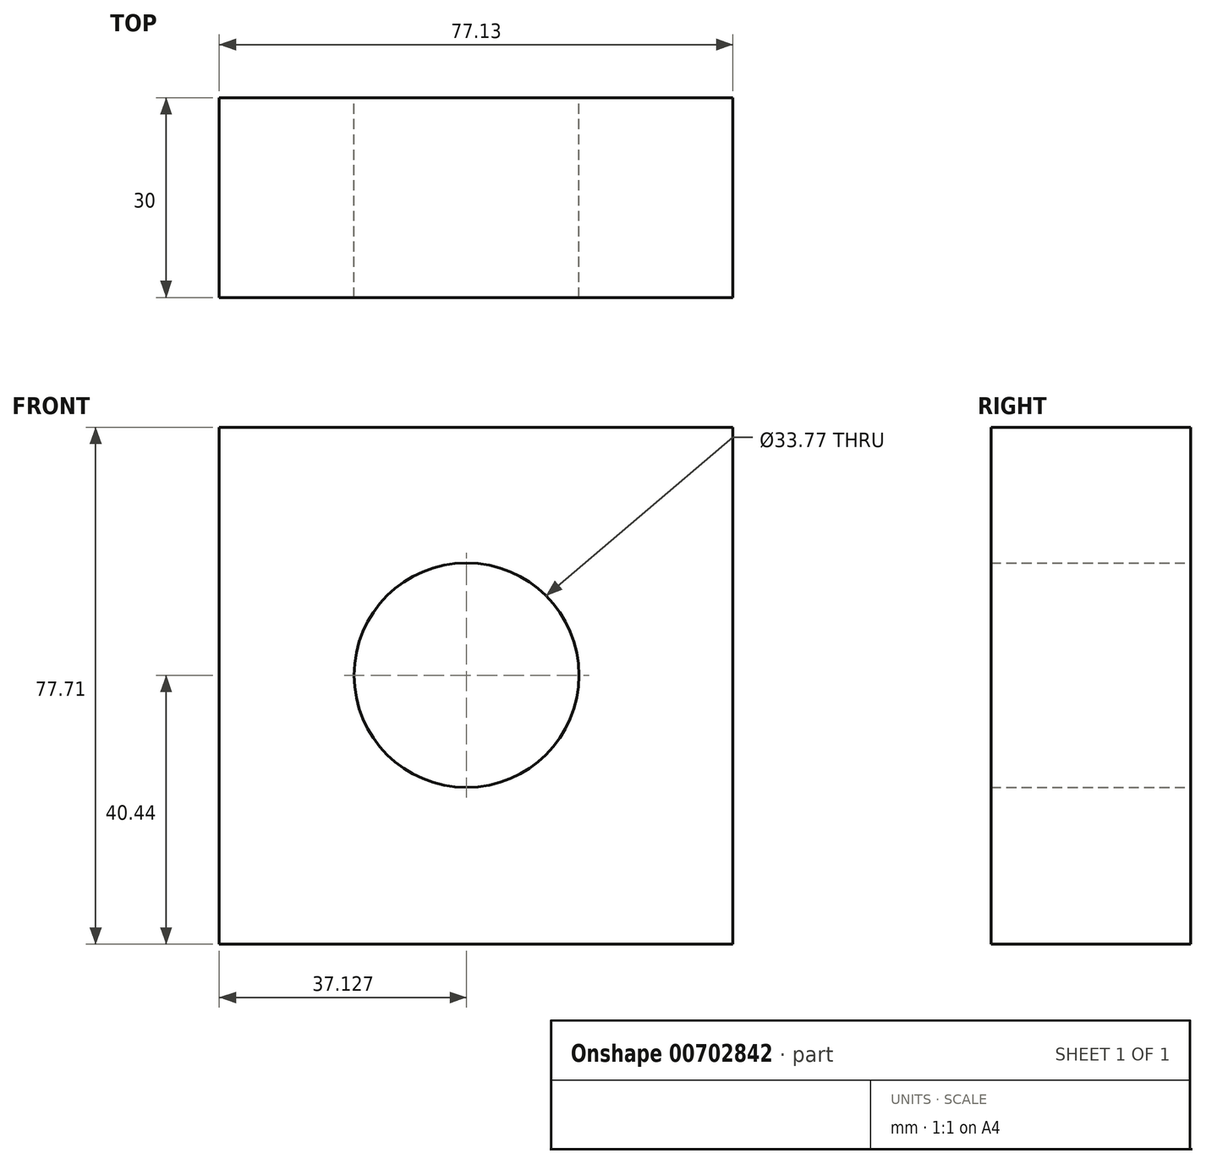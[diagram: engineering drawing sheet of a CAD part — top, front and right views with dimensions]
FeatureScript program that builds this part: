
annotation { "Feature Type Name" : "Feature", "Feature Type Description" : "" }
export const myFeature = defineFeature(function(context is Context, id is Id, definition is map)
    precondition{}
    {
        {
            var Q0;
            Q0=qCreatedBy(makeId("Front.planeOp"),FACE);
            var sketch = newSketch(context, id + "F0", { "sketchPlane" : qUnion([Q0])});
            skLineSegment(sketch, "E0", {"start": v(-53.1, 37.27) * mm, "end": v(-53.1, -40.44) * mm});
            skLineSegment(sketch, "E1", {"start": v(-53.1, -40.44) * mm, "end": v(24.03, -40.44) * mm});
            skLineSegment(sketch, "E2", {"start": v(24.03, -40.44) * mm, "end": v(24.03, 37.27) * mm});
            skLineSegment(sketch, "E3", {"start": v(24.03, 37.27) * mm, "end": v(-53.1, 37.27) * mm});
            skCircle(sketch, "E4", {"center": v(-15.97, 0) * mm, "radius": 16.88 * mm});
            skSolve(sketch);
        }
        {
            var Q0;
            Q0 = qSketchRegion(id + "F0", true);
            extrude(context, id + "F1", {"entities" : qUnion([Q0]), "depth" : 30 * mm, "offsetDistance" : 25 * mm});
        }
    });
